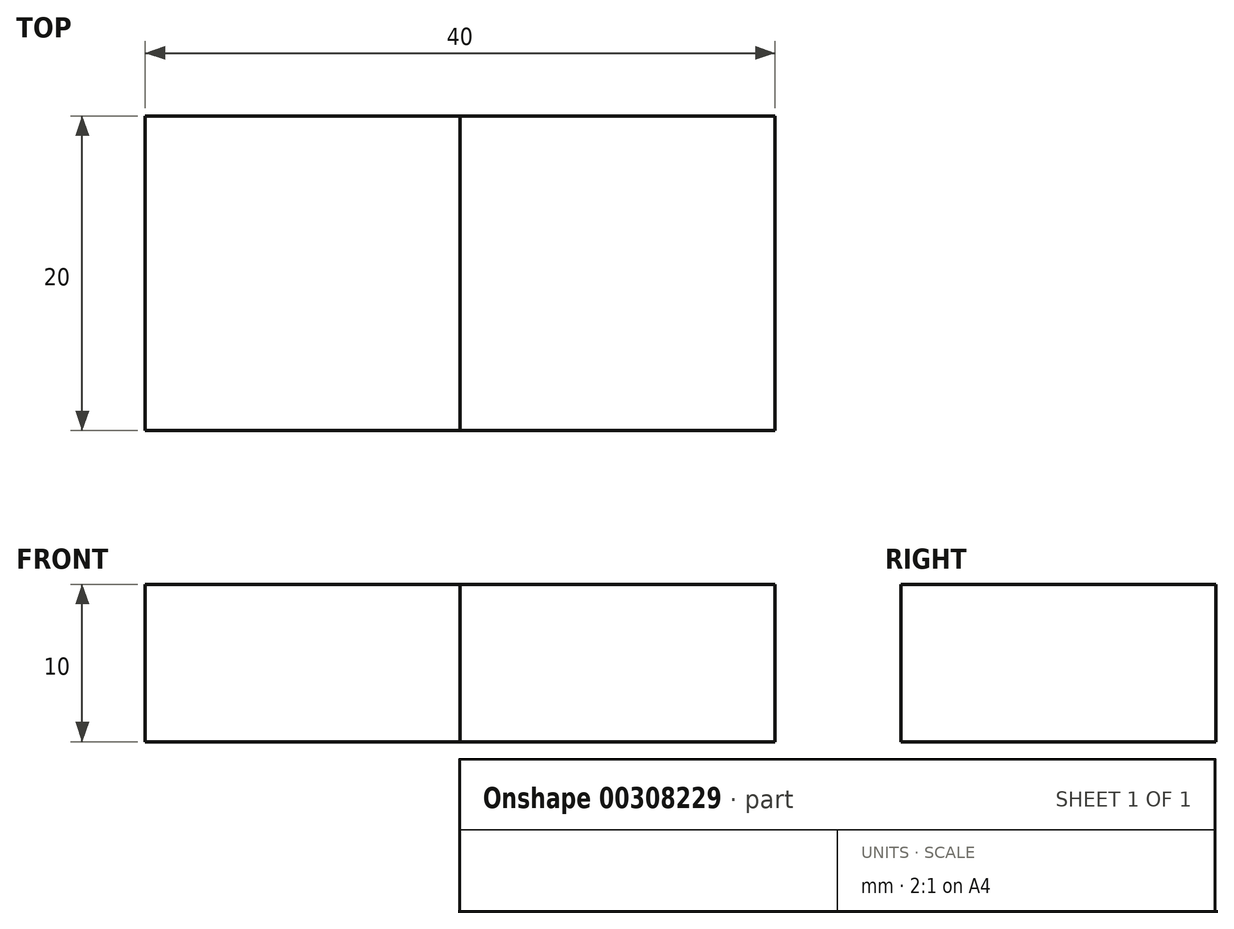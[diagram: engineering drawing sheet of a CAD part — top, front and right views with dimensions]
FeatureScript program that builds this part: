
annotation { "Feature Type Name" : "Feature", "Feature Type Description" : "" }
export const myFeature = defineFeature(function(context is Context, id is Id, definition is map)
    precondition{}
    {
        {
            var Q0;
            Q0=qCreatedBy(makeId("Top.planeOp"),FACE);
            var sketch = newSketch(context, id + "F0", { "sketchPlane" : qUnion([Q0])});
            skLineSegment(sketch, "E0.bottom", {"start": v(20, 10) * mm, "end": v(-20, 10) * mm});
            skLineSegment(sketch, "E0.top", {"start": v(20, -10) * mm, "end": v(-20, -10) * mm});
            skLineSegment(sketch, "E0.left", {"start": v(20, 10) * mm, "end": v(20, -10) * mm});
            skLineSegment(sketch, "E0.right", {"start": v(-20, 10) * mm, "end": v(-20, -10) * mm});
            skPoint(sketch, "E0.middle", {"position": v(0, 0) * mm});
            skLineSegment(sketch, "E1", {"start": v(0, -10) * mm, "end": v(0, 10) * mm});
            skSolve(sketch);
        }
        {
            var Q0;
            {var subQ0=sQuery(id+"F0.wireOp",EDGE,"E0.right");Q0=makeQuery(id+"F0.imprint","IMPRINT",FACE,{"disambiguationData":[TD([[makeQuery(id+"F0.imprint","IMPRINT",EDGE,{"derivedFrom":subQ0}),1.0]])]});}
            extrude(context, id + "F1", {"entities" : qUnion([Q0]), "depth" : 10 * mm, "offsetDistance" : 25 * mm});
        }
        {
            var Q0;
            {var subQ0=sQuery(id+"F0.wireOp",EDGE,"E0.left");Q0=makeQuery(id+"F0.imprint","IMPRINT",FACE,{"disambiguationData":[TD([[makeQuery(id+"F0.imprint","IMPRINT",EDGE,{"derivedFrom":subQ0}),-1.0]])]});}
            extrude(context, id + "F2", {"entities" : qUnion([Q0]), "depth" : 10 * mm, "offsetDistance" : 25 * mm});
        }
    });
